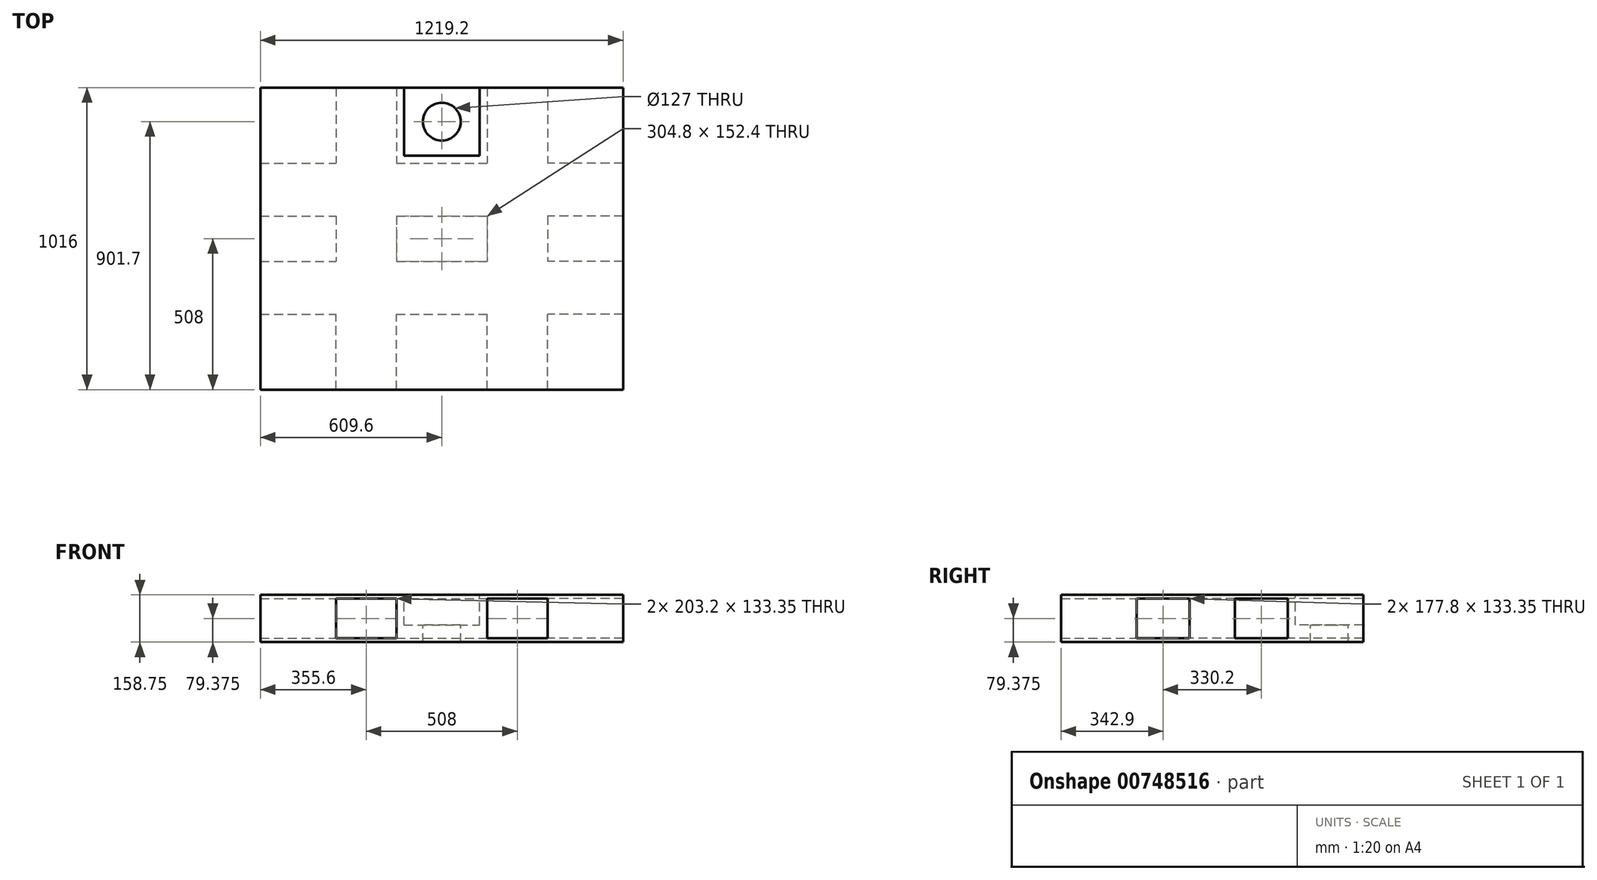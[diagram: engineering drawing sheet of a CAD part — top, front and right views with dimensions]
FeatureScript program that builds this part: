
annotation { "Feature Type Name" : "Feature", "Feature Type Description" : "" }
export const myFeature = defineFeature(function(context is Context, id is Id, definition is map)
    precondition{}
    {
        {
            var Q0;
            Q0=qCreatedBy(makeId("Top.planeOp"),FACE);
            var sketch = newSketch(context, id + "F0", { "sketchPlane" : qUnion([Q0])});
            skLineSegment(sketch, "E0.bottom", {"start": v(609.6, 508) * mm, "end": v(-609.6, 508) * mm});
            skLineSegment(sketch, "E0.top", {"start": v(609.6, -508) * mm, "end": v(-609.6, -508) * mm});
            skLineSegment(sketch, "E0.left", {"start": v(609.6, 508) * mm, "end": v(609.6, -508) * mm});
            skLineSegment(sketch, "E0.right", {"start": v(-609.6, 508) * mm, "end": v(-609.6, -508) * mm});
            skPoint(sketch, "E0.middle", {"position": v(0, 0) * mm});
            skSolve(sketch);
        }
        {
            var Q0;
            Q0=makeQuery(id+"F0.imprint","IMPRINT",FACE,{"disambiguationData":[TD([[makeQuery(id+"F0.imprint","IMPRINT",EDGE,{"derivedFrom":sQuery(id+"F0.wireOp",EDGE,"E0.bottom")}),1.0]])]});
            extrude(context, id + "F1", {"entities" : qUnion([Q0]), "depth" : 12.7 * mm, "offsetDistance" : 25.4 * mm});
        }
        {
            var Q0;
            Q0=makeQuery(id+"F1.opExtrude","CAP_FACE",FACE,{"disambiguationData":[OSD([sQuery(id+"F0.wireOp",EDGE,"E0.bottom"),sQuery(id+"F0.wireOp",EDGE,"E0.top"),sQuery(id+"F0.wireOp",EDGE,"E0.left"),sQuery(id+"F0.wireOp",EDGE,"E0.right")])],"isStart":false});
            var sketch = newSketch(context, id + "F2", { "sketchPlane" : qUnion([Q0])});
            skLineSegment(sketch, "E1.bottom", {"start": v(-609.6, 508) * mm, "end": v(-355.6, 508) * mm});
            skLineSegment(sketch, "E1.top", {"start": v(-609.6, 254) * mm, "end": v(-355.6, 254) * mm});
            skLineSegment(sketch, "E1.left", {"start": v(-609.6, 508) * mm, "end": v(-609.6, 254) * mm});
            skLineSegment(sketch, "E1.right", {"start": v(-355.6, 508) * mm, "end": v(-355.6, 254) * mm});
            skLineSegment(sketch, "E2.bottom", {"start": v(609.6, 508) * mm, "end": v(355.6, 508) * mm});
            skLineSegment(sketch, "E2.top", {"start": v(609.6, 254) * mm, "end": v(355.6, 254) * mm});
            skLineSegment(sketch, "E2.left", {"start": v(609.6, 508) * mm, "end": v(609.6, 254) * mm});
            skLineSegment(sketch, "E2.right", {"start": v(355.6, 508) * mm, "end": v(355.6, 254) * mm});
            skLineSegment(sketch, "E3.bottom", {"start": v(609.6, -508) * mm, "end": v(355.6, -508) * mm});
            skLineSegment(sketch, "E3.top", {"start": v(609.6, -254) * mm, "end": v(355.6, -254) * mm});
            skLineSegment(sketch, "E3.left", {"start": v(609.6, -508) * mm, "end": v(609.6, -254) * mm});
            skLineSegment(sketch, "E3.right", {"start": v(355.6, -508) * mm, "end": v(355.6, -254) * mm});
            skLineSegment(sketch, "E4.bottom", {"start": v(-609.6, -508) * mm, "end": v(-355.6, -508) * mm});
            skLineSegment(sketch, "E4.top", {"start": v(-609.6, -254) * mm, "end": v(-355.6, -254) * mm});
            skLineSegment(sketch, "E4.left", {"start": v(-609.6, -508) * mm, "end": v(-609.6, -254) * mm});
            skLineSegment(sketch, "E4.right", {"start": v(-355.6, -508) * mm, "end": v(-355.6, -254) * mm});
            skLineSegment(sketch, "E5.bottom", {"start": v(-152.4, 508) * mm, "end": v(152.4, 508) * mm});
            skLineSegment(sketch, "E5.top", {"start": v(-152.4, 254) * mm, "end": v(152.4, 254) * mm});
            skLineSegment(sketch, "E5.left", {"start": v(-152.4, 508) * mm, "end": v(-152.4, 254) * mm});
            skLineSegment(sketch, "E5.right", {"start": v(152.4, 508) * mm, "end": v(152.4, 254) * mm});
            skLineSegment(sketch, "E6.bottom", {"start": v(-152.4, -508) * mm, "end": v(152.4, -508) * mm});
            skLineSegment(sketch, "E6.top", {"start": v(-152.4, -254) * mm, "end": v(152.4, -254) * mm});
            skLineSegment(sketch, "E6.left", {"start": v(-152.4, -508) * mm, "end": v(-152.4, -254) * mm});
            skLineSegment(sketch, "E6.right", {"start": v(152.4, -508) * mm, "end": v(152.4, -254) * mm});
            skLineSegment(sketch, "E7.bottom", {"start": v(609.6, 76.2) * mm, "end": v(355.6, 76.2) * mm});
            skLineSegment(sketch, "E7.top", {"start": v(609.6, -76.2) * mm, "end": v(355.6, -76.2) * mm});
            skLineSegment(sketch, "E7.left", {"start": v(609.6, 76.2) * mm, "end": v(609.6, -76.2) * mm});
            skLineSegment(sketch, "E7.right", {"start": v(355.6, 76.2) * mm, "end": v(355.6, -76.2) * mm});
            skLineSegment(sketch, "E8.bottom", {"start": v(-609.6, 76.2) * mm, "end": v(-355.6, 76.2) * mm});
            skLineSegment(sketch, "E8.top", {"start": v(-609.6, -76.2) * mm, "end": v(-355.6, -76.2) * mm});
            skLineSegment(sketch, "E8.left", {"start": v(-609.6, 76.2) * mm, "end": v(-609.6, -76.2) * mm});
            skLineSegment(sketch, "E8.right", {"start": v(-355.6, 76.2) * mm, "end": v(-355.6, -76.2) * mm});
            skLineSegment(sketch, "E9.bottom", {"start": v(-152.4, 76.2) * mm, "end": v(152.4, 76.2) * mm});
            skLineSegment(sketch, "E9.top", {"start": v(-152.4, -76.2) * mm, "end": v(152.4, -76.2) * mm});
            skLineSegment(sketch, "E9.left", {"start": v(-152.4, 76.2) * mm, "end": v(-152.4, -76.2) * mm});
            skLineSegment(sketch, "E9.right", {"start": v(152.4, 76.2) * mm, "end": v(152.4, -76.2) * mm});
            skLineSegment(sketch, "E10", {"start": v(0, 0) * mm, "end": v(0, 76.2) * mm, "construction": true});
            skLineSegment(sketch, "E11", {"start": v(0, 0) * mm, "end": v(-152.4, 0) * mm, "construction": true});
            skSolve(sketch);
        }
        {
            var Q0;
            Q0 = qSketchRegion(id + "F2", true);
            extrude(context, id + "F3", {"entities" : qUnion([Q0]), "operationType" : NewBodyOperationType.ADD, "depth" : 133.35 * mm, "offsetDistance" : 25.4 * mm});
        }
        {
            var Q0;
            Q0=makeQuery(id+"F3.opExtrude","CAP_FACE",FACE,{"disambiguationData":[OSD([sQuery(id+"F2.wireOp",EDGE,"E1.bottom"),sQuery(id+"F2.wireOp",EDGE,"E1.top"),sQuery(id+"F2.wireOp",EDGE,"E1.left"),sQuery(id+"F2.wireOp",EDGE,"E1.right")])],"isStart":false});
            var sketch = newSketch(context, id + "F4", { "sketchPlane" : qUnion([Q0])});
            skLineSegment(sketch, "E12.bottom", {"start": v(-609.6, 508) * mm, "end": v(609.6, 508) * mm});
            skLineSegment(sketch, "E12.top", {"start": v(-609.6, -508) * mm, "end": v(609.6, -508) * mm});
            skLineSegment(sketch, "E12.left", {"start": v(-609.6, 508) * mm, "end": v(-609.6, -508) * mm});
            skLineSegment(sketch, "E12.right", {"start": v(609.6, 508) * mm, "end": v(609.6, -508) * mm});
            skSolve(sketch);
        }
        {
            var Q0;
            Q0 = qSketchRegion(id + "F4", true);
            extrude(context, id + "F5", {"entities" : qUnion([Q0]), "operationType" : NewBodyOperationType.ADD, "depth" : 12.7 * mm, "offsetDistance" : 25.4 * mm});
        }
        {
            var Q0;
            Q0=makeQuery(id+"F5.opExtrude","CAP_FACE",FACE,{"disambiguationData":[OSD([sQuery(id+"F4.wireOp",EDGE,"E12.bottom"),sQuery(id+"F4.wireOp",EDGE,"E12.top"),sQuery(id+"F4.wireOp",EDGE,"E12.left"),sQuery(id+"F4.wireOp",EDGE,"E12.right")])],"isStart":false});
            var sketch = newSketch(context, id + "F6", { "sketchPlane" : qUnion([Q0])});
            skLineSegment(sketch, "E13.bottom", {"start": v(-127, 508) * mm, "end": v(127, 508) * mm});
            skLineSegment(sketch, "E13.top", {"start": v(-127, 279.4) * mm, "end": v(127, 279.4) * mm});
            skLineSegment(sketch, "E13.left", {"start": v(-127, 508) * mm, "end": v(-127, 279.4) * mm});
            skLineSegment(sketch, "E13.right", {"start": v(127, 508) * mm, "end": v(127, 279.4) * mm});
            skLineSegment(sketch, "E14", {"start": v(0, 279.4) * mm, "end": v(0, -508) * mm, "construction": true});
            skSolve(sketch);
        }
        {
            var Q0;
            Q0 = qSketchRegion(id + "F6", true);
            extrude(context, id + "F7", {"entities" : qUnion([Q0]), "operationType" : NewBodyOperationType.REMOVE, "oppositeDirection" : true, "depth" : 101.6 * mm, "offsetDistance" : 25.4 * mm});
        }
        {
            var Q0;
            Q0=makeQuery(id+"F7.boolean.opBoolean","COPY",FACE,{"derivedFrom":makeQuery(id+"F7.opExtrude","CAP_FACE",FACE,{"disambiguationData":[OSD([sQuery(id+"F6.wireOp",EDGE,"E13.bottom"),sQuery(id+"F6.wireOp",EDGE,"E13.top"),sQuery(id+"F6.wireOp",EDGE,"E13.left"),sQuery(id+"F6.wireOp",EDGE,"E13.right")])],"isStart":false})});
            var sketch = newSketch(context, id + "F8", { "sketchPlane" : qUnion([Q0])});
            skLineSegment(sketch, "E15", {"start": v(-127, 508) * mm, "end": v(127, 279.4) * mm, "construction": true});
            skCircle(sketch, "E16", {"center": v(0, 393.7) * mm, "radius": 107.95 * mm, "construction": true});
            skCircle(sketch, "E17", {"center": v(0, 393.7) * mm, "radius": 63.5 * mm});
            skSolve(sketch);
        }
        {
            var Q0;
            Q0 = qSketchRegion(id + "F8", true);
            extrude(context, id + "F9", {"entities" : qUnion([Q0]), "operationType" : NewBodyOperationType.REMOVE, "endBound" : BoundingType.THROUGH_ALL, "oppositeDirection" : true, "depth" : 25.4 * mm, "offsetDistance" : 25.4 * mm});
        }
    });
